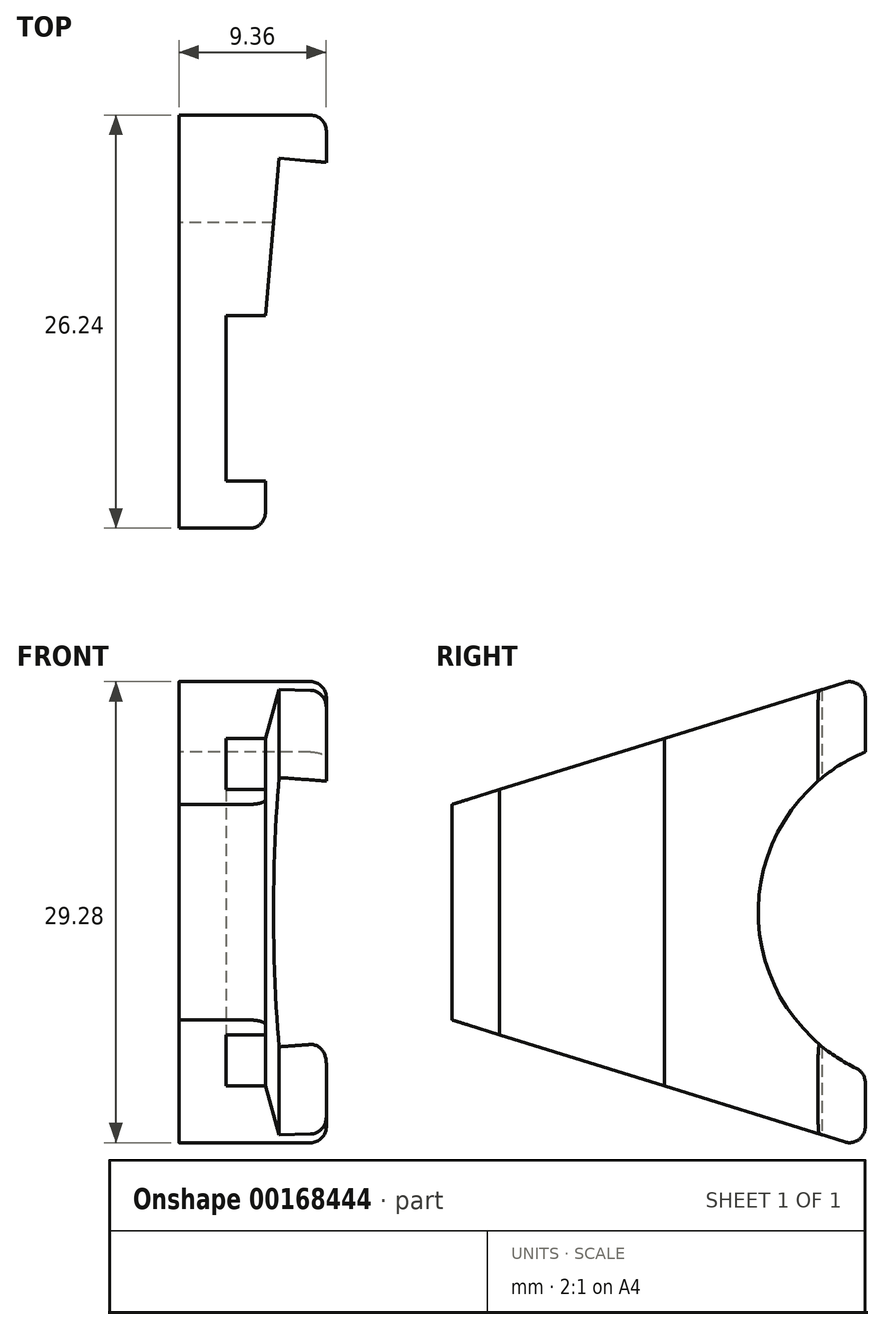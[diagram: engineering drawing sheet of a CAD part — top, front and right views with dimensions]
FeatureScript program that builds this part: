
annotation { "Feature Type Name" : "Feature", "Feature Type Description" : "" }
export const myFeature = defineFeature(function(context is Context, id is Id, definition is map)
    precondition{}
    {
        {
            var Q0;
            Q0=qCreatedBy(makeId("Top.planeOp"),FACE);
            var sketch = newSketch(context, id + "F0", { "sketchPlane" : qUnion([Q0])});
            skLineSegment(sketch, "E0", {"start": v(0.87, 11.88) * mm, "end": v(3.86, 11.62) * mm});
            skLineSegment(sketch, "E1", {"start": v(3.86, 11.62) * mm, "end": v(3.86, 14.62) * mm});
            skLineSegment(sketch, "E2", {"start": v(3.86, 14.62) * mm, "end": v(-5.5, 14.62) * mm});
            skLineSegment(sketch, "E3", {"start": v(-5.5, 14.62) * mm, "end": v(-5.5, -11.62) * mm});
            skLineSegment(sketch, "E4", {"start": v(-5.5, -11.62) * mm, "end": v(0, -11.62) * mm});
            skLineSegment(sketch, "E5", {"start": v(0, -11.62) * mm, "end": v(0, -8.62) * mm});
            skLineSegment(sketch, "E6", {"start": v(0, -8.62) * mm, "end": v(-2.5, -8.62) * mm});
            skLineSegment(sketch, "E7", {"start": v(-2.5, -8.62) * mm, "end": v(-2.5, 1.88) * mm});
            skLineSegment(sketch, "E8", {"start": v(-2.5, 1.88) * mm, "end": v(0, 1.88) * mm});
            skLineSegment(sketch, "E9", {"start": v(0.87, 11.88) * mm, "end": v(0, 1.88) * mm});
            skSolve(sketch);
        }
        {
            var Q0;
            Q0=makeQuery(id+"F0.imprint","IMPRINT",FACE,{"disambiguationData":[TD([[makeQuery(id+"F0.imprint","IMPRINT",EDGE,{"derivedFrom":sQuery(id+"F0.wireOp",EDGE,"E0")}),1.0]])]});
            extrude(context, id + "F1", {"entities" : qUnion([Q0]), "endBound" : BoundingType.SYMMETRIC, "depth" : 30 * mm});
        }
        {
            var Q0;
            Q0=makeQuery(id+"F1.opExtrude","SWEPT_FACE",FACE,{"disambiguationData":[OSD([sQuery(id+"F0.wireOp",EDGE,"E3")])]});
            var sketch = newSketch(context, id + "F2", { "sketchPlane" : qUnion([Q0])});
            skLineSegment(sketch, "E10.0", {"start": v(-14.62, 15) * mm, "end": v(-14.62, -15) * mm});
            skLineSegment(sketch, "E11.0", {"start": v(11.62, 15) * mm, "end": v(11.62, -15) * mm});
            skArc(sketch, "E12", {"start": v(-14.62, -10.18) * mm, "mid": v(-7.8, 0) * mm, "end": v(-14.62, 10.18) * mm});
            skLineSegment(sketch, "E13", {"start": v(-14.62, -15) * mm, "end": v(11.62, -6.85) * mm});
            skLineSegment(sketch, "E14", {"start": v(-14.62, 0) * mm, "end": v(11.62, 0) * mm, "construction": true});
            skLineSegment(sketch, "E15.MirrorCS", {"start": v(-14.62, 15) * mm, "end": v(11.62, 6.85) * mm});
            skSolve(sketch);
        }
        {
            var Q0;
            {var subQ2=sQuery(id+"F2.wireOp",EDGE,"E13");Q0=makeQuery(id+"F2.imprint","IMPRINT",FACE,{"disambiguationData":[TD([[makeQuery(id+"F2.imprint","IMPRINT",EDGE,{"derivedFrom":subQ2}),-1.0]])]});}
            var Q1;
            {var subQ2=sQuery(id+"F2.wireOp",EDGE,"E15.MirrorCS");Q1=makeQuery(id+"F2.imprint","IMPRINT",FACE,{"disambiguationData":[TD([[makeQuery(id+"F2.imprint","IMPRINT",EDGE,{"derivedFrom":subQ2}),1.0]])]});}
            var Q2;
            {var subQ0=sQuery(id+"F2.wireOp",EDGE,"E12");Q2=makeQuery(id+"F2.imprint","IMPRINT",FACE,{"disambiguationData":[TD([[makeQuery(id+"F2.imprint","IMPRINT",EDGE,{"derivedFrom":subQ0}),1.0]])]});}
            extrude(context, id + "F3", {"entities" : qUnion([Q0, Q1, Q2]), "operationType" : NewBodyOperationType.REMOVE, "endBound" : BoundingType.THROUGH_ALL, "oppositeDirection" : true, "depth" : 25 * mm});
        }
        {
            var Q0;
            Q0=makeQuery(id+"F3.boolean.opBoolean","MERGE",EDGE,{"derivedFrom":[makeQuery(id+"F1.opExtrude","CAP_EDGE",EDGE,{"disambiguationData":[OSD([sQuery(id+"F0.wireOp",EDGE,"E2")])],"isStart":false}),makeQuery(id+"F3.opExtrude","SWEPT_EDGE",EDGE,{"disambiguationData":[OSD([sQuery(id+"F0.wireOp",EDGE,"E3"),sQuery(id+"F2.wireOp",EDGE,"E10.0"),sQuery(id+"F2.wireOp",EDGE,"E15.MirrorCS")])]})]});
            var Q1;
            {var subQ0=sQuery(id+"F2.wireOp",EDGE,"E12");var subQ1=sQuery(id+"F2.wireOp",EDGE,"E10.0");Q1=makeQuery(id+"F3.boolean.opBoolean","COPY",EDGE,{"derivedFrom":makeQuery(id+"F3.opExtrude","SWEPT_EDGE",EDGE,{"disambiguationData":[OSD([subQ1,subQ0]),TDD([makeQuery(id+"F2.imprint","INTERSECT",VERTEX,{"disambiguationData":[OD(1.0)],"derivedFrom":[subQ1,subQ0]})])]})});}
            var Q2;
            {var subQ0=sQuery(id+"F2.wireOp",EDGE,"E12");var subQ1=sQuery(id+"F2.wireOp",EDGE,"E10.0");Q2=makeQuery(id+"F3.boolean.opBoolean","COPY",EDGE,{"derivedFrom":makeQuery(id+"F3.opExtrude","SWEPT_EDGE",EDGE,{"disambiguationData":[OSD([subQ1,subQ0]),TDD([makeQuery(id+"F2.imprint","INTERSECT",VERTEX,{"disambiguationData":[OD(0.0)],"derivedFrom":[subQ1,subQ0]})])]})});}
            var Q3;
            Q3=makeQuery(id+"F3.boolean.opBoolean","MERGE",EDGE,{"derivedFrom":[makeQuery(id+"F1.opExtrude","CAP_EDGE",EDGE,{"disambiguationData":[OSD([sQuery(id+"F0.wireOp",EDGE,"E2")])],"isStart":true}),makeQuery(id+"F3.opExtrude","SWEPT_EDGE",EDGE,{"disambiguationData":[OSD([sQuery(id+"F0.wireOp",EDGE,"E3"),sQuery(id+"F2.wireOp",EDGE,"E10.0"),sQuery(id+"F2.wireOp",EDGE,"E13")])]})]});
            var Q4;
            Q4=makeQuery(id+"F3.boolean.opBoolean","COPY",EDGE,{"derivedFrom":makeQuery(id+"F3.opExtrude","SWEPT_EDGE",EDGE,{"disambiguationData":[OSD([sQuery(id+"F2.wireOp",EDGE,"E11.0"),sQuery(id+"F2.wireOp",EDGE,"E13")])]})});
            var Q5;
            Q5=makeQuery(id+"F3.boolean.opBoolean","COPY",EDGE,{"derivedFrom":makeQuery(id+"F3.opExtrude","SWEPT_EDGE",EDGE,{"disambiguationData":[OSD([sQuery(id+"F2.wireOp",EDGE,"E11.0"),sQuery(id+"F2.wireOp",EDGE,"E15.MirrorCS")])]})});
            fillet(context, id + "F4", {"entities" : qUnion([Q0, Q1, Q2, Q3, Q4, Q5]), "radius" : 1 * mm, "tangentPropagation" : true, "allowEdgeOverflow" : false});
        }
        {
            var Q0;
            {var subQ0=sQuery(id+"F0.wireOp",EDGE,"E1");var subQ1=sQuery(id+"F0.wireOp",EDGE,"E2");Q0=makeQuery(id+"F3.boolean.opBoolean","SPLIT",EDGE,{"disambiguationData":[TD([makeQuery(id+"F3.opExtrude","SWEPT_FACE",FACE,{"disambiguationData":[OSD([sQuery(id+"F2.wireOp",EDGE,"E13")])]})])],"derivedFrom":makeQuery(id+"F1.opExtrude","SWEPT_EDGE",EDGE,{"disambiguationData":[OSD([subQ0,subQ1])]})});}
            var Q1;
            {var subQ0=sQuery(id+"F0.wireOp",EDGE,"E1");var subQ1=sQuery(id+"F0.wireOp",EDGE,"E2");Q1=makeQuery(id+"F3.boolean.opBoolean","SPLIT",EDGE,{"disambiguationData":[TD([makeQuery(id+"F3.opExtrude","SWEPT_FACE",FACE,{"disambiguationData":[OSD([sQuery(id+"F2.wireOp",EDGE,"E15.MirrorCS")])]})])],"derivedFrom":makeQuery(id+"F1.opExtrude","SWEPT_EDGE",EDGE,{"disambiguationData":[OSD([subQ0,subQ1])]})});}
            var Q2;
            Q2=makeQuery(id+"F1.opExtrude","SWEPT_EDGE",EDGE,{"disambiguationData":[OSD([sQuery(id+"F0.wireOp",EDGE,"E4"),sQuery(id+"F0.wireOp",EDGE,"E5")])]});
            fillet(context, id + "F5", {"entities" : qUnion([Q0, Q1, Q2]), "radius" : 1 * mm, "tangentPropagation" : true, "allowEdgeOverflow" : false});
        }
    });
